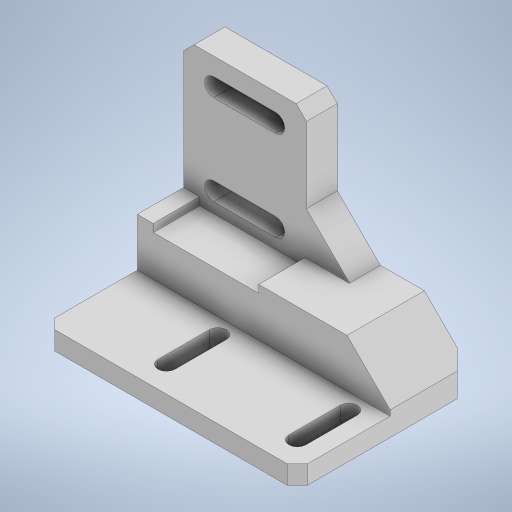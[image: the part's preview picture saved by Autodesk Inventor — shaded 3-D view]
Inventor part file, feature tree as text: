
AUTODESK INVENTOR PART (.ipt)
format: ipt  version: 2024 (Build 280153020, 153B)  size: 370,176 bytes
history: native  units: in
note: dims shown in document units (in); Inventor stores cm internally (conversion verified against a paired STEP export)
features: sketch x12, extrude x10, chamfer x4, projected_geometry x2
ambient origin geometry x8: Origin, YZ Plane, XZ Plane, XY Plane, X Axis, Y Axis, Z Axis, Center Point
bodies: Solid1 (feature_tree)
feature tree (28):
  extrude  "Extrusion1"  Depth=1.063in
  extrude  "Extrusion2"  Depth=0.2362in
  extrude  "Extrusion3"  Depth=1.4961in TaperAngle=0.0deg
  sketch  "Sketch4"  dims[d8=0.1969in d9=0.1969in]
  extrude  "Extrusion6"  Depth=0.1969in
  extrude  "Extrusion8"  Depth=1.0in
  sketch  "Sketch10"  dims[d31=0.4724in d32=0.4724in]
  extrude  "Extrusion7"  Depth=0.3937in
  extrude  "Extrusion9"  Depth=0.2976in
  extrude  "Extrusion5"  Depth=0.689in
  extrude  "Extrusion10"  Depth=0.4724in
  chamfer  "Chamfer5"  Distance=1.405in
  extrude  "Extrusion11"  Depth=0.7087in
  chamfer  "Chamfer6"  Distance=0.4724in
  chamfer  "Chamfer7"  Distance=0.3937in
  chamfer  "Chamfer8"  Distance=0.0591in
  sketch  "Sketch1"  dims[d0=0.5118in d1=1.063in]
  sketch  "Sketch2"  dims[d2=1.5748in d3=0.0in d4=0.2362in]
  sketch  "Sketch3"  dims[d5=1.4961in d6=1.5748in d7=0.0in]
  sketch  "Sketch6"  dims[d10=0.3937in d11=1.0in]
  sketch  "Sketch7"  dims[d12=0.1299in d13=0.1969in d14=0.3937in d15=1.0in d16=0.1299in]
  sketch  "Sketch8"  dims[d17=1.5748in d18=0.0in d28=0.2976in]
  sketch  "Sketch9"  dims[d29=0.689in d30=0.1575in]
  sketch  "Sketch11"  dims[d33=0.1378in]
  projected_geometry  "Projected Loop1"
  sketch  "Sketch13"  dims[d34=0.1378in d35=1.405in d36=0.0in]
  sketch  "Sketch14"  dims[d37=1.7825in d38=0.0in d53=0.0984in d54=0.4724in d55=0.3937in d56=0.0591in d57=0.0in d58=0.1417in d59=0.7087in d60=1.9813in d61=0.0in d62=0.3563in d63=0.0in d64=0.3563in d65=0.0in d66=0.3287in d67=0.0787in d68=45.0deg d69=0.2062in d70=0.0in d71=0.3287in d72=0.0787in d73=45.0deg d74=0.0787in d75=0.0787in d76=45.0deg d77=0.0787in d78=0.0787in d79=45.0deg]
  projected_geometry  "Projected Loop2"
